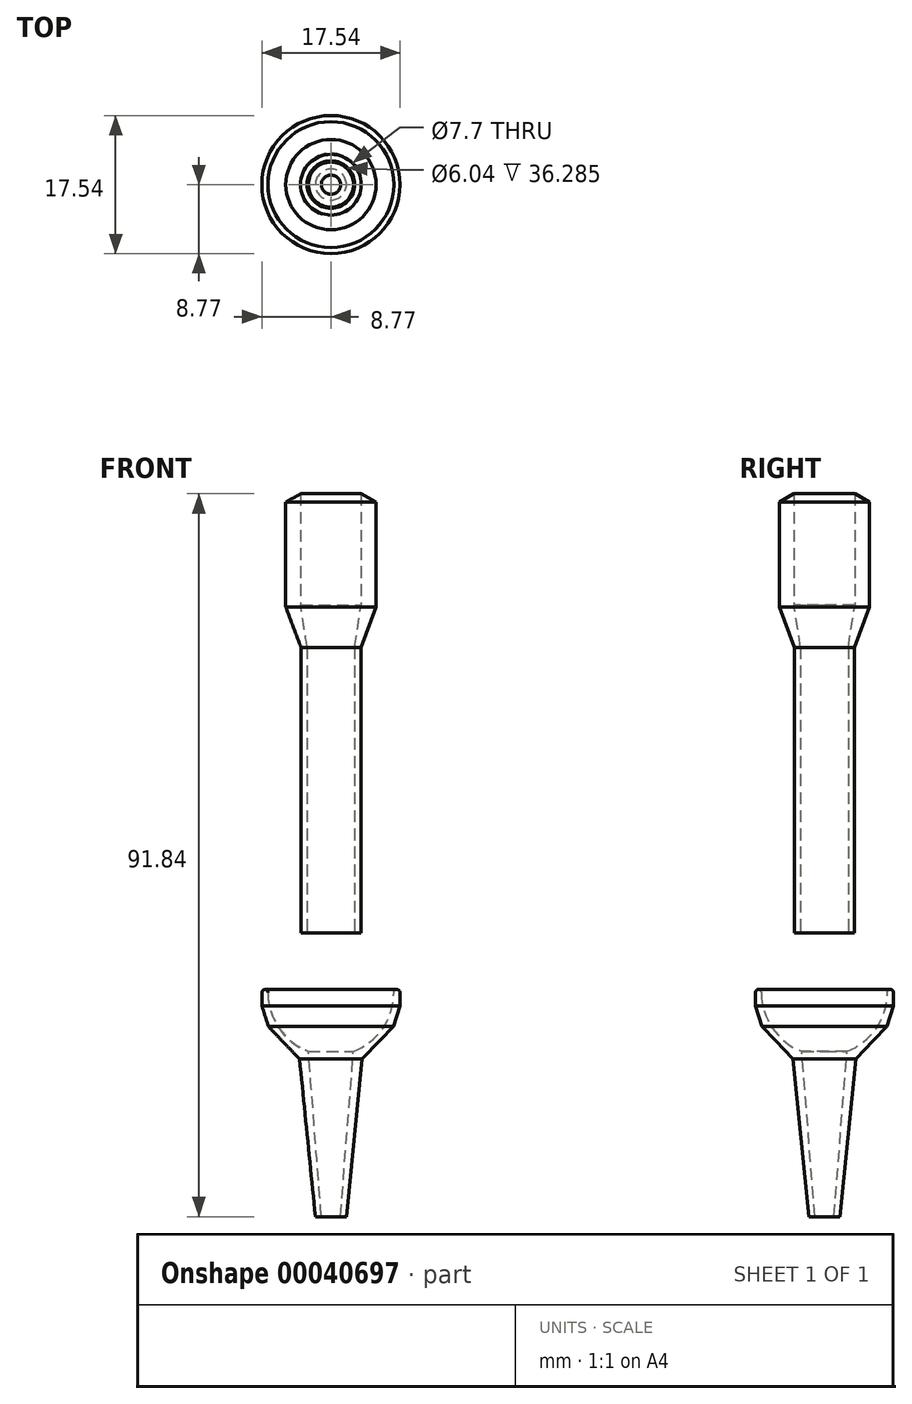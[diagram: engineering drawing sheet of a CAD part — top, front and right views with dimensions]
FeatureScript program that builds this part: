
annotation { "Feature Type Name" : "Feature", "Feature Type Description" : "" }
export const myFeature = defineFeature(function(context is Context, id is Id, definition is map)
    precondition{}
    {
        {
            var Q0;
            Q0=qCreatedBy(makeId("Front.planeOp"),FACE);
            var sketch = newSketch(context, id + "F0", { "sketchPlane" : qUnion([Q0])});
            skArc(sketch, "E0", {"start": v(8, 0) * mm, "mid": v(6.6, -4.53) * mm, "end": v(2.86, -7.47) * mm});
            skLineSegment(sketch, "E1", {"start": v(2.86, -7.47) * mm, "end": v(1.22, -28.41) * mm});
            skLineSegment(sketch, "E2", {"start": v(1.22, -28.41) * mm, "end": v(1.97, -28.47) * mm});
            skLineSegment(sketch, "E3", {"start": v(1.97, -28.47) * mm, "end": v(3.98, -8.44) * mm});
            skLineSegment(sketch, "E4", {"start": v(3.98, -8.44) * mm, "end": v(6.23, -6.1) * mm});
            skLineSegment(sketch, "E5", {"start": v(6.23, -6.1) * mm, "end": v(7.92, -4.31) * mm});
            skLineSegment(sketch, "E6", {"start": v(7.92, -4.31) * mm, "end": v(8.77, -1.69) * mm});
            skLineSegment(sketch, "E7", {"start": v(8.77, -1.69) * mm, "end": v(8.77, 0) * mm});
            skArc(sketch, "E8", {"start": v(8.77, 0) * mm, "mid": v(8.38, 0.38) * mm, "end": v(8, 0) * mm});
            skLineSegment(sketch, "E9", {"start": v(0, -28.48) * mm, "end": v(0, 0) * mm});
            skSolve(sketch);
        }
        {
            var Q0;
            Q0 = qSketchRegion(id + "F0", true);
            var Q1;
            Q1=sQuery(id+"F0.wireOp",EDGE,"E9");
            revolve(context, id + "F1", {"entities" : qUnion([Q0]), "axis" : qUnion([Q1]), "revolveType" : RevolveType.FULL});
        }
        {
            var Q0;
            Q0=qCreatedBy(makeId("Front.planeOp"),FACE);
            var sketch = newSketch(context, id + "F2", { "sketchPlane" : qUnion([Q0])});
            skLineSegment(sketch, "E10", {"start": v(3.85, 63.37) * mm, "end": v(3.85, 49.22) * mm});
            skLineSegment(sketch, "E11", {"start": v(3.85, 49.22) * mm, "end": v(3.02, 43.85) * mm});
            skLineSegment(sketch, "E12", {"start": v(3.02, 43.85) * mm, "end": v(3.02, 7.56) * mm});
            skLineSegment(sketch, "E13", {"start": v(3.02, 7.56) * mm, "end": v(3.8, 7.56) * mm});
            skLineSegment(sketch, "E14", {"start": v(3.8, 43.85) * mm, "end": v(5.74, 48.98) * mm});
            skLineSegment(sketch, "E15", {"start": v(5.74, 48.98) * mm, "end": v(5.74, 62.29) * mm});
            skLineSegment(sketch, "E16", {"start": v(5.74, 62.29) * mm, "end": v(3.85, 63.37) * mm});
            skLineSegment(sketch, "E17", {"start": v(0, 7.84) * mm, "end": v(0, 62.29) * mm});
            skLineSegment(sketch, "E18", {"start": v(3.8, 7.56) * mm, "end": v(3.8, 43.85) * mm});
            skSolve(sketch);
        }
        {
            var Q0;
            Q0=makeQuery(id+"F2.imprint","IMPRINT",FACE,{"disambiguationData":[TD([[makeQuery(id+"F2.imprint","IMPRINT",EDGE,{"derivedFrom":sQuery(id+"F2.wireOp",EDGE,"E10")}),1.0]])]});
            var Q1;
            Q1=sQuery(id+"F2.wireOp",EDGE,"E17");
            revolve(context, id + "F3", {"entities" : qUnion([Q0]), "axis" : qUnion([Q1]), "revolveType" : RevolveType.FULL});
        }
        {
            var Q0;
            Q0=qCreatedBy(makeId("Top.planeOp"),FACE);
            var sketch = newSketch(context, id + "F4", { "sketchPlane" : qUnion([Q0])});
            skCircle(sketch, "E19", {"center": v(34.3, 0) * mm, "radius": 3.53 * mm});
            skCircle(sketch, "E20", {"center": v(34.3, 0) * mm, "radius": 2.87 * mm});
            skSolve(sketch);
        }
        {
            var Q0;
            Q0=qCreatedBy(makeId("Front.planeOp"),FACE);
            var sketch = newSketch(context, id + "F5", { "sketchPlane" : qUnion([Q0])});
            skArc(sketch, "E21", {"start": v(138.12, 0) * mm, "mid": v(86.02, 114.9) * mm, "end": v(33.91, 0) * mm});
            skSolve(sketch);
        }
    });
